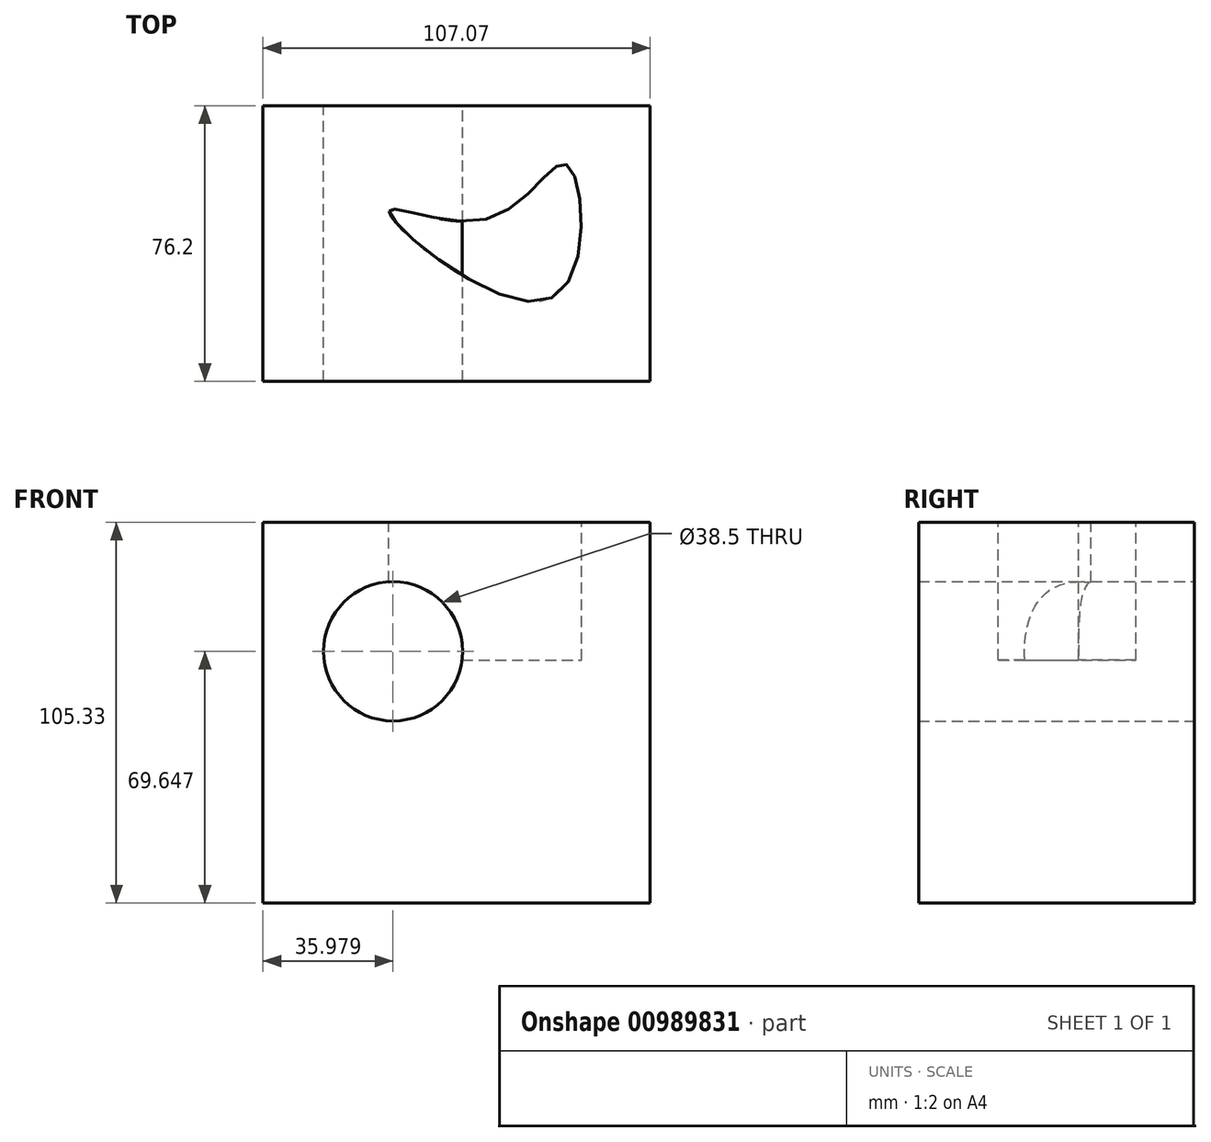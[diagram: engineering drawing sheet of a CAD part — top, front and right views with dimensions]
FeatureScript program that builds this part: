
annotation { "Feature Type Name" : "Feature", "Feature Type Description" : "" }
export const myFeature = defineFeature(function(context is Context, id is Id, definition is map)
    precondition{}
    {
        {
            var Q0;
            Q0=qCreatedBy(makeId("Front.planeOp"),FACE);
            var sketch = newSketch(context, id + "F0", { "sketchPlane" : qUnion([Q0])});
            skLineSegment(sketch, "E0.bottom", {"start": v(-49.65, 52.52) * mm, "end": v(57.42, 52.52) * mm});
            skLineSegment(sketch, "E0.top", {"start": v(-49.65, -52.81) * mm, "end": v(57.42, -52.81) * mm});
            skLineSegment(sketch, "E0.left", {"start": v(-49.65, 52.52) * mm, "end": v(-49.65, -52.81) * mm});
            skLineSegment(sketch, "E0.right", {"start": v(57.42, 52.52) * mm, "end": v(57.42, -52.81) * mm});
            skCircle(sketch, "E1", {"center": v(-13.67, 16.84) * mm, "radius": 19.25 * mm});
            skSolve(sketch);
        }
        {
            var Q0;
            Q0=makeQuery(id+"F0.imprint","IMPRINT",FACE,{"disambiguationData":[TD([[makeQuery(id+"F0.imprint","IMPRINT",EDGE,{"derivedFrom":sQuery(id+"F0.wireOp",EDGE,"E0.bottom")}),-1.0]])]});
            extrude(context, id + "F1", {"entities" : qUnion([Q0]), "depth" : 76.2 * mm, "offsetDistance" : 25.4 * mm});
        }
        {
            var Q0;
            Q0=makeQuery(id+"F1.opExtrude","SWEPT_FACE",FACE,{"disambiguationData":[OSD([sQuery(id+"F0.wireOp",EDGE,"E0.bottom")])]});
            var sketch = newSketch(context, id + "F2", { "sketchPlane" : qUnion([Q0])});
            skFitSpline(sketch, "E2", {"points": [v(-14.8, -29.26) * mm, v(29.95, -53.29) * mm, v(34.6, -16.49) * mm, v(13, -31.16) * mm, v(-14.8, -29.26) * mm]});
            skSolve(sketch);
        }
        {
            var Q0;
            Q0=makeQuery(id+"F2.imprint","IMPRINT",FACE,{"disambiguationData":[TD([[makeQuery(id+"F2.imprint","IMPRINT",EDGE,{"derivedFrom":sQuery(id+"F2.wireOp",EDGE,"E2")}),1.0]])]});
            extrude(context, id + "F3", {"entities" : qUnion([Q0]), "operationType" : NewBodyOperationType.REMOVE, "oppositeDirection" : true, "depth" : 38.1 * mm, "offsetDistance" : 25.4 * mm});
        }
    });
